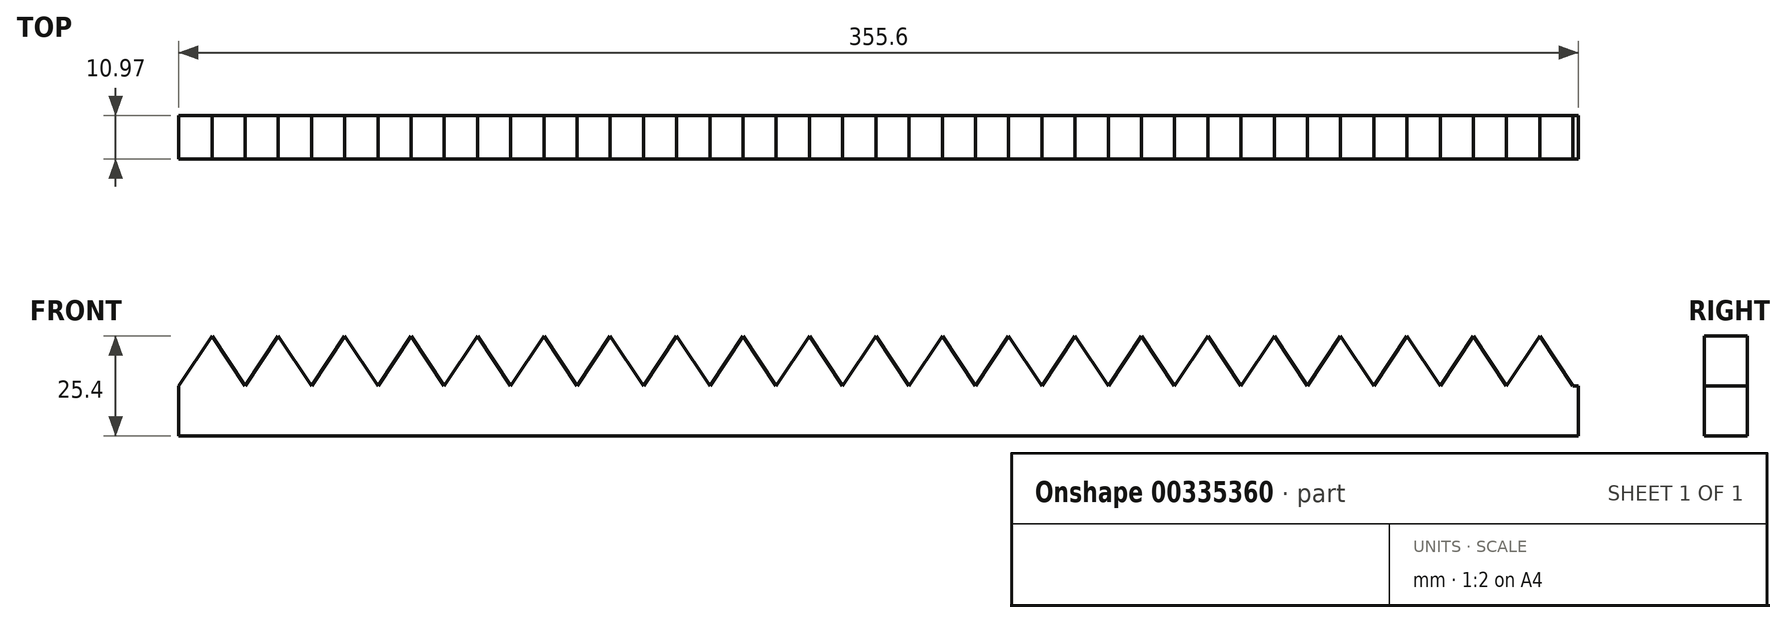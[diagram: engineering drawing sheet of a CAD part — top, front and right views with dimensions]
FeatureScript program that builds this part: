
annotation { "Feature Type Name" : "Feature", "Feature Type Description" : "" }
export const myFeature = defineFeature(function(context is Context, id is Id, definition is map)
    precondition{}
    {
        {
            var Q0;
            Q0=qCreatedBy(makeId("Front.planeOp"),FACE);
            var sketch = newSketch(context, id + "F0", { "sketchPlane" : qUnion([Q0])});
            skLineSegment(sketch, "E0.top", {"start": v(-177.67, -22.78) * mm, "end": v(177.93, -22.78) * mm});
            skLineSegment(sketch, "E0.left", {"start": v(-177.67, -10.08) * mm, "end": v(-177.67, -22.78) * mm});
            skLineSegment(sketch, "E0.right", {"start": v(177.93, -10.08) * mm, "end": v(177.93, -22.78) * mm});
            skLineSegment(sketch, "E1", {"start": v(-177.67, -10.08) * mm, "end": v(177.93, -10.08) * mm});
            skLineSegment(sketch, "E2", {"start": v(-177.67, -10.08) * mm, "end": v(-169.23, 2.62) * mm});
            skLineSegment(sketch, "E3", {"start": v(-169.23, 2.62) * mm, "end": v(-160.8, -10.08) * mm});
            skLineSegment(sketch, "E4.1.0.0", {"start": v(-152.36, 2.62) * mm, "end": v(-143.93, -10.08) * mm});
            skLineSegment(sketch, "E4.1.0.1", {"start": v(-160.8, -10.08) * mm, "end": v(-152.36, 2.62) * mm});
            skLineSegment(sketch, "E4.2.0.0", {"start": v(-135.49, 2.62) * mm, "end": v(-127.07, -10.08) * mm});
            skLineSegment(sketch, "E4.2.0.1", {"start": v(-143.93, -10.08) * mm, "end": v(-135.49, 2.62) * mm});
            skLineSegment(sketch, "E4.3.0.0", {"start": v(-118.62, 2.62) * mm, "end": v(-110.2, -10.08) * mm});
            skLineSegment(sketch, "E4.3.0.1", {"start": v(-127.07, -10.08) * mm, "end": v(-118.62, 2.62) * mm});
            skLineSegment(sketch, "E4.4.0.0", {"start": v(-101.75, 2.62) * mm, "end": v(-93.33, -10.08) * mm});
            skLineSegment(sketch, "E4.4.0.1", {"start": v(-110.2, -10.08) * mm, "end": v(-101.75, 2.62) * mm});
            skLineSegment(sketch, "E4.5.0.0", {"start": v(-84.89, 2.62) * mm, "end": v(-76.46, -10.08) * mm});
            skLineSegment(sketch, "E4.5.0.1", {"start": v(-93.33, -10.08) * mm, "end": v(-84.89, 2.62) * mm});
            skLineSegment(sketch, "E4.6.0.0", {"start": v(-68.02, 2.62) * mm, "end": v(-59.6, -10.08) * mm});
            skLineSegment(sketch, "E4.6.0.1", {"start": v(-76.46, -10.08) * mm, "end": v(-68.02, 2.62) * mm});
            skLineSegment(sketch, "E4.7.0.0", {"start": v(-51.15, 2.62) * mm, "end": v(-42.72, -10.08) * mm});
            skLineSegment(sketch, "E4.7.0.1", {"start": v(-59.6, -10.08) * mm, "end": v(-51.15, 2.62) * mm});
            skLineSegment(sketch, "E4.8.0.0", {"start": v(-34.28, 2.62) * mm, "end": v(-25.86, -10.08) * mm});
            skLineSegment(sketch, "E4.8.0.1", {"start": v(-42.73, -10.08) * mm, "end": v(-34.28, 2.62) * mm});
            skLineSegment(sketch, "E4.9.0.0", {"start": v(-17.41, 2.62) * mm, "end": v(-8.99, -10.08) * mm});
            skLineSegment(sketch, "E4.9.0.1", {"start": v(-25.86, -10.08) * mm, "end": v(-17.41, 2.62) * mm});
            skLineSegment(sketch, "E4.10.0.0", {"start": v(-0.54, 2.62) * mm, "end": v(7.88, -10.08) * mm});
            skLineSegment(sketch, "E4.10.0.1", {"start": v(-8.99, -10.08) * mm, "end": v(-0.54, 2.62) * mm});
            skLineSegment(sketch, "E4.11.0.0", {"start": v(16.32, 2.62) * mm, "end": v(24.75, -10.08) * mm});
            skLineSegment(sketch, "E4.11.0.1", {"start": v(7.88, -10.08) * mm, "end": v(16.32, 2.62) * mm});
            skLineSegment(sketch, "E4.12.0.0", {"start": v(33.2, 2.62) * mm, "end": v(41.62, -10.08) * mm});
            skLineSegment(sketch, "E4.12.0.1", {"start": v(24.75, -10.08) * mm, "end": v(33.2, 2.62) * mm});
            skLineSegment(sketch, "E4.13.0.0", {"start": v(50.06, 2.62) * mm, "end": v(58.48, -10.08) * mm});
            skLineSegment(sketch, "E4.13.0.1", {"start": v(41.61, -10.08) * mm, "end": v(50.06, 2.62) * mm});
            skLineSegment(sketch, "E4.14.0.0", {"start": v(66.93, 2.62) * mm, "end": v(75.35, -10.08) * mm});
            skLineSegment(sketch, "E4.14.0.1", {"start": v(58.48, -10.08) * mm, "end": v(66.93, 2.62) * mm});
            skLineSegment(sketch, "E4.15.0.0", {"start": v(83.8, 2.62) * mm, "end": v(92.22, -10.08) * mm});
            skLineSegment(sketch, "E4.15.0.1", {"start": v(75.35, -10.08) * mm, "end": v(83.8, 2.62) * mm});
            skLineSegment(sketch, "E4.16.0.0", {"start": v(100.66, 2.62) * mm, "end": v(109.09, -10.08) * mm});
            skLineSegment(sketch, "E4.16.0.1", {"start": v(92.22, -10.08) * mm, "end": v(100.66, 2.62) * mm});
            skLineSegment(sketch, "E4.17.0.0", {"start": v(117.53, 2.62) * mm, "end": v(125.96, -10.08) * mm});
            skLineSegment(sketch, "E4.17.0.1", {"start": v(109.09, -10.08) * mm, "end": v(117.53, 2.62) * mm});
            skLineSegment(sketch, "E4.18.0.0", {"start": v(134.4, 2.62) * mm, "end": v(142.82, -10.08) * mm});
            skLineSegment(sketch, "E4.18.0.1", {"start": v(125.96, -10.08) * mm, "end": v(134.4, 2.62) * mm});
            skLineSegment(sketch, "E4.19.0.0", {"start": v(151.27, 2.62) * mm, "end": v(159.7, -10.08) * mm});
            skLineSegment(sketch, "E4.19.0.1", {"start": v(142.82, -10.08) * mm, "end": v(151.27, 2.62) * mm});
            skLineSegment(sketch, "E4.20.0.0", {"start": v(168.14, 2.62) * mm, "end": v(176.56, -10.08) * mm});
            skLineSegment(sketch, "E4.20.0.1", {"start": v(159.7, -10.08) * mm, "end": v(168.14, 2.62) * mm});
            skLineSegment(sketch, "E4.direction1", {"start": v(-177.67, -10.08) * mm, "end": v(-160.8, -10.08) * mm, "construction": true});
            skSolve(sketch);
        }
        {
            var Q0;
            Q0 = qSketchRegion(id + "F0", true);
            extrude(context, id + "F1", {"entities" : qUnion([Q0]), "depth" : 10.97 * mm});
        }
    });
